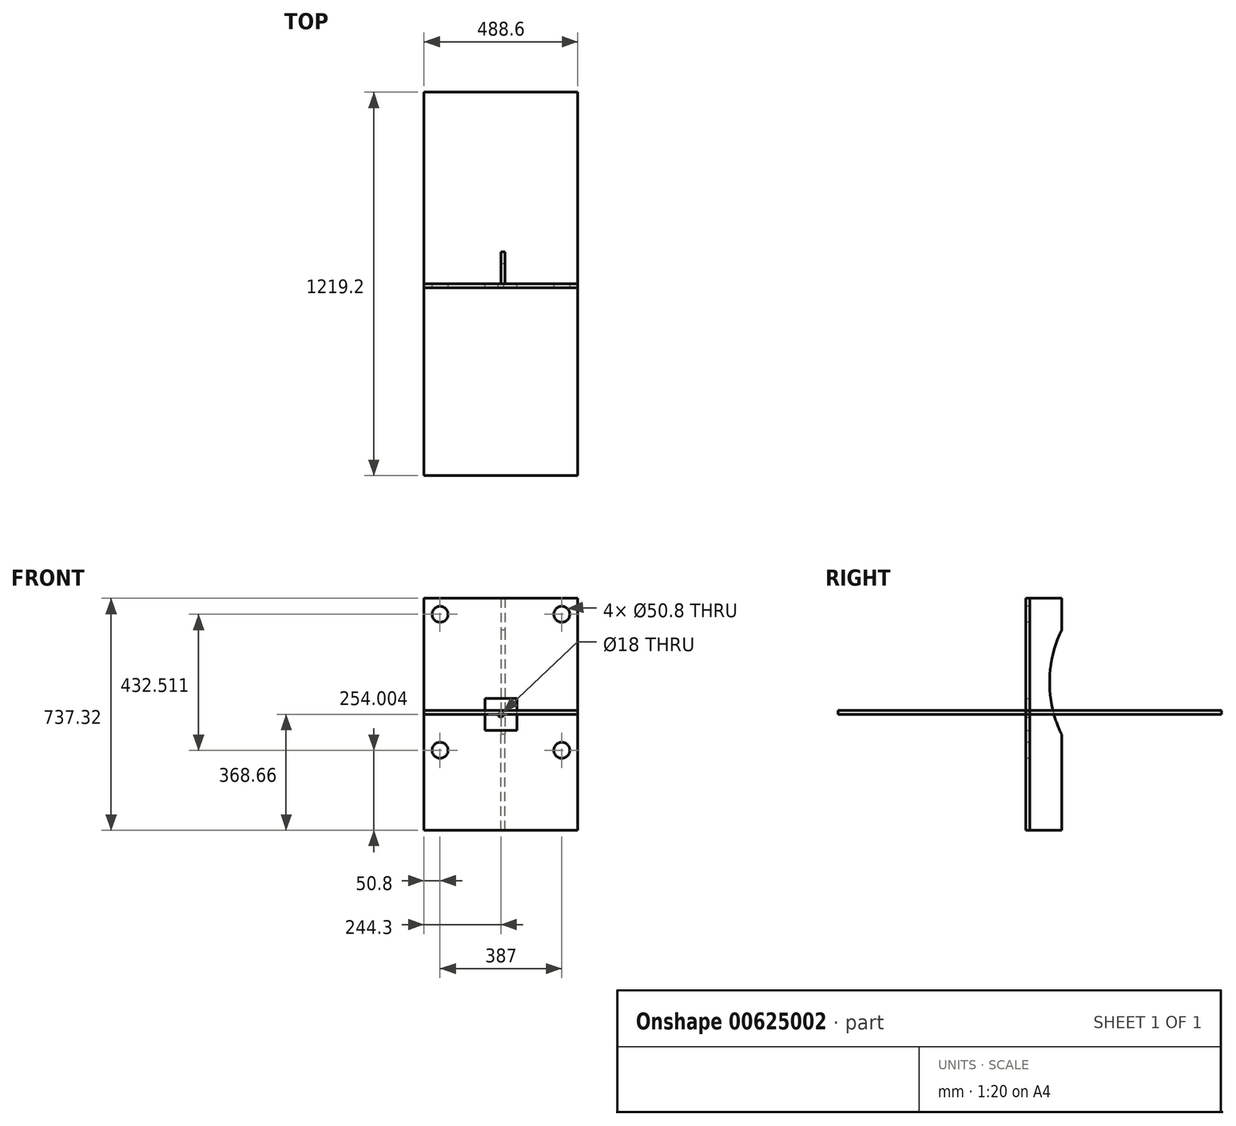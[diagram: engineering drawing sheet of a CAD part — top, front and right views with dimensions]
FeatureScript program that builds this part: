
annotation { "Feature Type Name" : "Feature", "Feature Type Description" : "" }
export const myFeature = defineFeature(function(context is Context, id is Id, definition is map)
    precondition{}
    {
        {
            assignVariable(context, id + "F0", {"name" : "steelthickness", "anyValue" : 12.7 * mm});
        }
        {
            var Q0;
            Q0=qCreatedBy(makeId("Front.planeOp"),FACE);
            var sketch = newSketch(context, id + "F1", { "sketchPlane" : qUnion([Q0])});
            skLineSegment(sketch, "E0.bottom", {"start": v(50.8, -50.8) * mm, "end": v(-50.8, -50.8) * mm});
            skLineSegment(sketch, "E0.top", {"start": v(50.8, 50.8) * mm, "end": v(-50.8, 50.8) * mm});
            skLineSegment(sketch, "E0.left", {"start": v(50.8, -50.8) * mm, "end": v(50.8, 50.8) * mm});
            skLineSegment(sketch, "E0.right", {"start": v(-50.8, -50.8) * mm, "end": v(-50.8, 50.8) * mm});
            skPoint(sketch, "E0.middle", {"position": v(0, 0) * mm});
            skCircle(sketch, "E1", {"center": v(0, 0) * mm, "radius": 9 * mm});
            skSolve(sketch);
        }
        {
            var Q0;
            Q0 = qSketchRegion(id + "F1", true);
            extrude(context, id + "F2", {"entities" : qUnion([Q0]), "depth" : getVariable(context, 'steelthickness'), "offsetDistance" : 25 * mm});
        }
        {
            var Q0;
            Q0=qCreatedBy(makeId("Right.planeOp"),FACE);
            var sketch = newSketch(context, id + "F3", { "sketchPlane" : qUnion([Q0])});
            skLineSegment(sketch, "E2", {"start": v(0, 368.66) * mm, "end": v(0, -368.66) * mm});
            skLineSegment(sketch, "E3", {"start": v(0, -368.66) * mm, "end": v(101.6, -368.66) * mm});
            skLineSegment(sketch, "E4", {"start": v(101.6, -368.66) * mm, "end": v(101.6, -63.86) * mm});
            skLineSegment(sketch, "E5", {"start": v(0, 368.66) * mm, "end": v(101.6, 368.66) * mm});
            skLineSegment(sketch, "E6", {"start": v(101.6, 368.66) * mm, "end": v(101.6, 267.06) * mm});
            skLineSegment(sketch, "E7", {"start": v(-97.43, 0) * mm, "end": v(147.45, 0) * mm, "construction": true});
            skArc(sketch, "E8", {"start": v(101.6, 267.06) * mm, "mid": v(63.5, 101.6) * mm, "end": v(101.6, -63.86) * mm});
            skLineSegment(sketch, "E9", {"start": v(101.6, 267.06) * mm, "end": v(101.6, -63.86) * mm, "construction": true});
            skSolve(sketch);
        }
        {
            var Q0;
            Q0 = qSketchRegion(id + "F3", true);
            extrude(context, id + "F4", {"entities" : qUnion([Q0]), "depth" : getVariable(context, 'steelthickness'), "offsetDistance" : 25 * mm});
        }
        {
            var Q0;
            Q0=qCreatedBy(makeId("Front.planeOp"),FACE);
            var sketch = newSketch(context, id + "F5", { "sketchPlane" : qUnion([Q0])});
            skLineSegment(sketch, "E10.bottom", {"start": v(244.3, -368.65) * mm, "end": v(-244.3, -368.66) * mm});
            skLineSegment(sketch, "E10.top", {"start": v(244.3, 368.66) * mm, "end": v(-244.3, 368.66) * mm});
            skLineSegment(sketch, "E10.left", {"start": v(244.3, -368.65) * mm, "end": v(244.3, 368.66) * mm});
            skLineSegment(sketch, "E10.right", {"start": v(-244.3, -368.66) * mm, "end": v(-244.3, 368.65) * mm});
            skPoint(sketch, "E10.middle", {"position": v(0, 0) * mm});
            skSolve(sketch);
        }
        {
            var Q0;
            Q0 = qSketchRegion(id + "F5", true);
            extrude(context, id + "F6", {"entities" : qUnion([Q0]), "depth" : getVariable(context, 'steelthickness'), "offsetDistance" : 25 * mm});
        }
        {
            var Q0;
            Q0=qCreatedBy(makeId("Top.planeOp"),FACE);
            var sketch = newSketch(context, id + "F7", { "sketchPlane" : qUnion([Q0])});
            skLineSegment(sketch, "E11.bottom", {"start": v(244.3, -609.6) * mm, "end": v(-244.3, -609.6) * mm});
            skLineSegment(sketch, "E11.top", {"start": v(244.3, 609.6) * mm, "end": v(-244.3, 609.6) * mm});
            skLineSegment(sketch, "E11.left", {"start": v(244.3, -609.6) * mm, "end": v(244.3, 609.6) * mm});
            skLineSegment(sketch, "E11.right", {"start": v(-244.3, -609.6) * mm, "end": v(-244.3, 609.6) * mm});
            skPoint(sketch, "E11.middle", {"position": v(0, 0) * mm});
            skSolve(sketch);
        }
        {
            var Q0;
            Q0 = qSketchRegion(id + "F7", true);
            extrude(context, id + "F8", {"entities" : qUnion([Q0]), "depth" : getVariable(context, 'steelthickness'), "offsetDistance" : 25 * mm});
        }
        {
            var Q0;
            Q0=makeQuery(id+"F6.opExtrude","CAP_FACE",FACE,{"disambiguationData":[OSD([sQuery(id+"F5.wireOp",EDGE,"E10.bottom"),sQuery(id+"F5.wireOp",EDGE,"E10.top"),sQuery(id+"F5.wireOp",EDGE,"E10.left"),sQuery(id+"F5.wireOp",EDGE,"E10.right")])],"isStart":false});
            var sketch = newSketch(context, id + "F9", { "sketchPlane" : qUnion([Q0])});
            skLineSegment(sketch, "E12.bottom", {"start": v(193.5, -114.66) * mm, "end": v(-193.5, -114.66) * mm, "construction": true});
            skLineSegment(sketch, "E12.top", {"start": v(193.5, 317.86) * mm, "end": v(-193.5, 317.86) * mm, "construction": true});
            skLineSegment(sketch, "E12.left", {"start": v(193.5, -114.66) * mm, "end": v(193.5, 317.86) * mm, "construction": true});
            skLineSegment(sketch, "E12.right", {"start": v(-193.5, -114.66) * mm, "end": v(-193.5, 317.86) * mm, "construction": true});
            skPoint(sketch, "E12.middle", {"position": v(0, 101.6) * mm});
            skLineSegment(sketch, "E13", {"start": v(0, 368.66) * mm, "end": v(0, 0) * mm, "construction": true});
            skCircle(sketch, "E14", {"center": v(-193.5, 317.86) * mm, "radius": 25.4 * mm});
            skLineSegment(sketch, "E15", {"start": v(-193.5, 101.6) * mm, "end": v(193.5, 101.6) * mm, "construction": true});
            skCircle(sketch, "E16.MirrorC", {"center": v(193.5, 317.86) * mm, "radius": 25.4 * mm});
            skCircle(sketch, "E17.MirrorC", {"center": v(-193.5, -114.66) * mm, "radius": 25.4 * mm});
            skCircle(sketch, "E18.MirrorC", {"center": v(193.5, -114.66) * mm, "radius": 25.4 * mm});
            skSolve(sketch);
        }
        {
            var Q0;
            Q0 = qSketchRegion(id + "F9", true);
            extrude(context, id + "F10", {"entities" : qUnion([Q0]), "operationType" : NewBodyOperationType.REMOVE, "endBound" : BoundingType.THROUGH_ALL, "oppositeDirection" : true, "depth" : 25 * mm, "offsetDistance" : 25 * mm});
        }
    });
